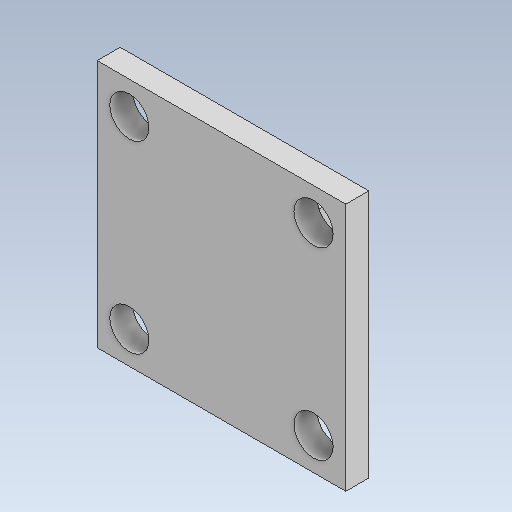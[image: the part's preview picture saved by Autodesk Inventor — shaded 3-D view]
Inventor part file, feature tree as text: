
AUTODESK INVENTOR PART (.ipt)
format: ipt  version: 2025.2 (Build 292293000, 293)  size: 330,240 bytes
history: native  units: mm
features: chamfer x4, sketch x3, extrude x2, hole x1
ambient origin geometry x8: Origin, YZ Plane, XZ Plane, XY Plane, X Axis, Y Axis, Z Axis, Center Point
bodies: Volumenkörper1 (feature_tree)
feature tree (10):
  extrude  "Extrusion1"  Depth=6.8mm
  extrude  "Extrusion2"  Depth=5.0mm TaperAngle=0.0deg
  hole  "Bohrung1"  [1 undecoded]
  chamfer  "Fasen5"  Distance=16.0mm
  chamfer  "Fasen6"  Distance=14.0mm
  chamfer  "Fasen7"  Distance=54.0mm
  chamfer  "Fasen8"  Distance=54.0mm
  sketch  "Skizze1"  dims[d2=6.8mm d3=6.8mm]
  sketch  "Skizze2"  dims[d7=10.0mm d8=0.0mm d9=5.0mm d10=0.0mm]
  sketch  "Skizze4"  dims[d11=16.0mm d12=14.0mm d13=16.0mm d14=14.0mm d35=54.0mm d36=54.0mm d37=8.5mm d38=6.0mm d39=4.0mm d40=2.0mm d41=90.0deg d42=5.0mm d43=0.0mm d44=7.0mm d45=7.0mm d46=7.0mm d47=7.0mm d48=7.0mm d49=7.0mm d50=7.0mm d51=7.0mm d52=40.0mm d53=40.0mm d54=40.0mm d55=40.0mm d56=26.0mm d57=22.0mm d58=6.8mm d59=6.8mm d61=5.0mm d62=5.0mm d63=5.0mm d65=1.8mm d66=0.2mm d67=5.0mm d68=10.0mm d69=2.0mm d70=3.804818mm d71=10.0mm d72=2.0mm d73=3.804818mm d74=10.0mm d75=2.0mm d76=3.804818mm d77=10.0mm d78=2.0mm d79=3.804818mm]
note: 1 required parameter value undecoded (feature->parameter linkage not recoverable at this tier; creation-order binding heuristic only, values carry confidence <= 0.55)
